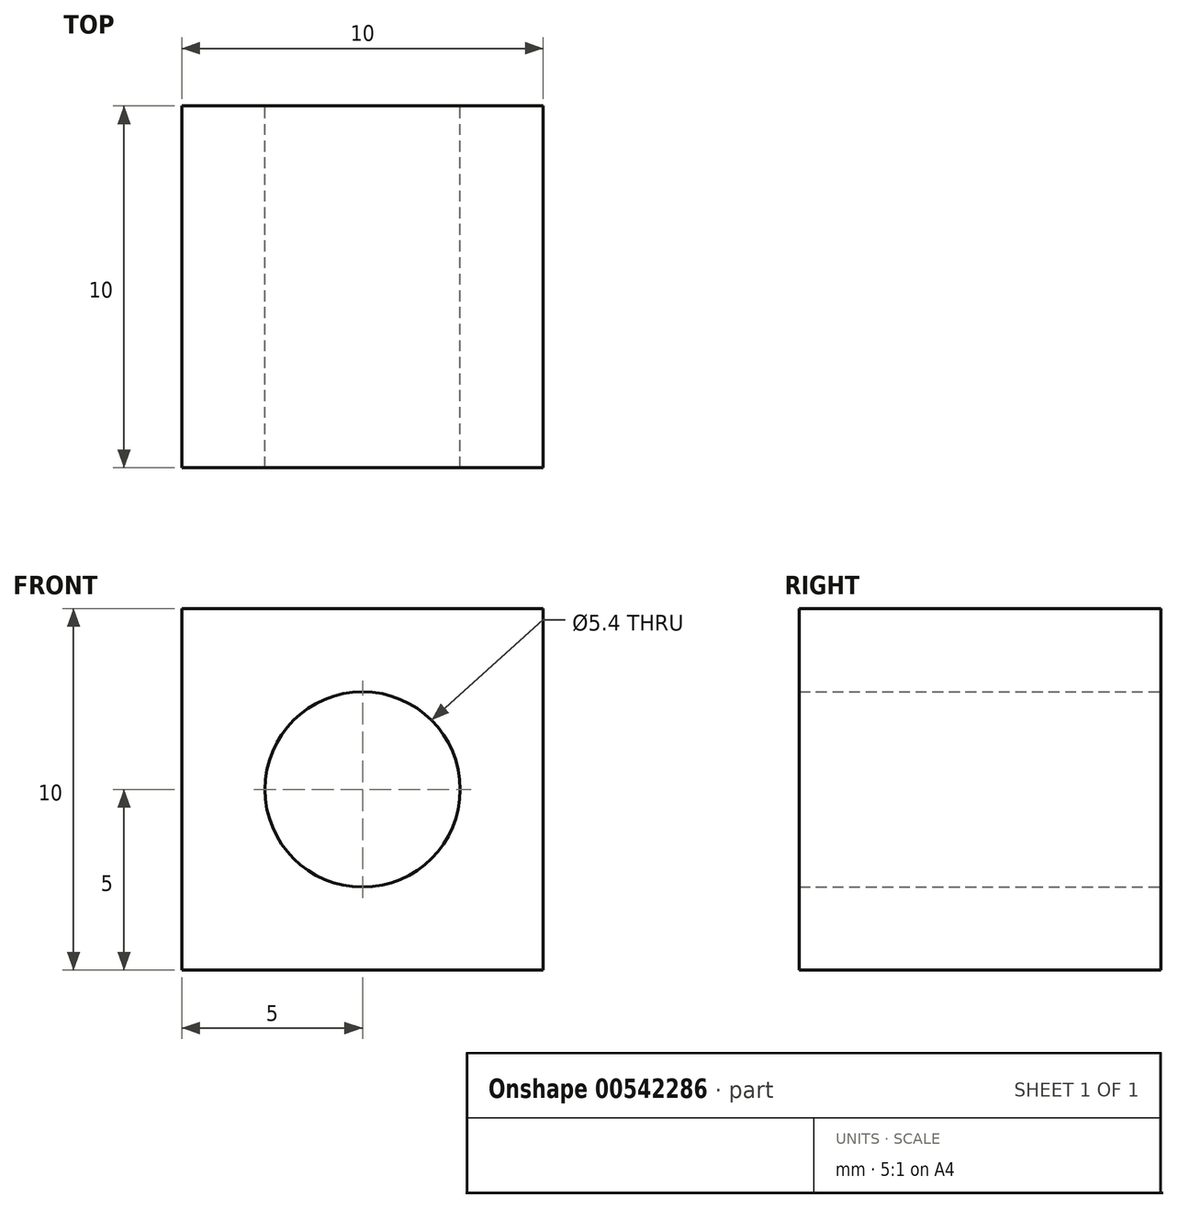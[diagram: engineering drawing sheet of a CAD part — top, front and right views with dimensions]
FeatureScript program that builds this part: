
annotation { "Feature Type Name" : "Feature", "Feature Type Description" : "" }
export const myFeature = defineFeature(function(context is Context, id is Id, definition is map)
    precondition{}
    {
        {
            var Q0;
            Q0=qCreatedBy(makeId("Front.planeOp"),FACE);
            var sketch = newSketch(context, id + "F0", { "sketchPlane" : qUnion([Q0])});
            skLineSegment(sketch, "E0.bottom", {"start": v(0, 5) * mm, "end": v(10, 5) * mm});
            skLineSegment(sketch, "E0.top", {"start": v(0, -5) * mm, "end": v(10, -5) * mm});
            skLineSegment(sketch, "E0.right", {"start": v(10, 5) * mm, "end": v(10, -5) * mm});
            skPoint(sketch, "E0.middle", {"position": v(0, 0) * mm});
            skLineSegment(sketch, "E1", {"start": v(0, 5) * mm, "end": v(0, -5) * mm});
            skCircle(sketch, "E2.MirrorC", {"center": v(5, 0) * mm, "radius": 2.7 * mm});
            skSolve(sketch);
        }
        {
            var Q0;
            Q0=makeQuery(id+"F0.imprint","IMPRINT",FACE,{"disambiguationData":[TD([[makeQuery(id+"F0.imprint","IMPRINT",EDGE,{"derivedFrom":sQuery(id+"F0.wireOp",EDGE,"E0.bottom")}),-1.0]])]});
            extrude(context, id + "F1", {"entities" : qUnion([Q0]), "depth" : 10 * mm, "offsetDistance" : 25 * mm});
        }
    });
